# Revit family: Hager-FW-IP30-Without_Door-With_notch-vuoto-CH-it
name_source: partatom
category: Electrical Equipment
units: mm (PartAtom-declared; Revit-internal decimal feet)

## family parameters
Cut with Voids When Loaded = No
Host = Face
Panel Configuration = Two Columns, Circuits Across
Part Type = Panelboard
Room Calculation Point = No
Round Connector Dimension = Use Diameter
Shared = No

## types (16) — shared parameters
EF000003 - Tipo di montaggio = EV000128 - parete forata
EF000007 - colore = EV000202 - bianco
EF000049 - profondità = 125 mm  [stored 0.410105 ft]
EF000118 - con piastra di montaggio = No
EF000218 - profondità di incasso = 112 mm  [stored 0.367454 ft]
EF000339 - tipo di copertura = EV000494 - senza
EF001062 - esecuzione EMC = No
EF001088 - possibilità di applicazione = Yes
EF001131 - profondità interna = 112 mm  [stored 0.367454 ft]
EF001134 - barra DIN = Yes
EF001596 - Attacco Lampada = EV000179 - acciaio
EF004462 - tipo di chiusura = EV000154 - altri
EF005474 - grado di protezione (IP) = EV006410 - IP30
EF006244 - coperchio/porta trasparente = Yes
EF006306 - con serratura = No
EF009212 - esecuzione coperchio = EV009916 - con taglio
EF015776 - Morsettiera di terra = No
EF015777 - Morsettiera neutra = No
EF015941 - Segnale di passaggio porta = No
HG000002 - Con porta = No
HG000003 - Gamma = FW
HG000005 - Spessore = 3 mm  [stored 0.00984252 ft]
HG000006 - Ad incasso = Yes
HG000009 - Porta doppia a battente = No
HG000010 - Porte asimmetriche = No
HG000011 - File vuote nella parte basse = No
HG000017 - Distanza tra i poli = 18 mm  [stored 0.0590551 ft]
Manufacturer = Hager
Type Comments = FW
zero-valued in all types: Default Elevation, EF000266 - numero di file, EF002950 - Numero moduli DIN, HG000001 - Numero di colonne, HG000007 - Numero di colonne vuote, HG000008 - Numero di file vuote

## per-type parameters (varying)
| type | EF000008 - Larghezza | EF000040 - Altezza | EF000332 - Altezza della parte incassata | EF000846 - larghezza di montaggio | HG000004 - Codice produttore | Model |
| incassato IP30 L353 A1003 P125 0 Unità di divisione - FWU61L | 353 mm  [stored 1.15814 ft] | 1003 mm  [stored 3.29068 ft] | 952 mm  [stored 3.12336 ft] | 310 mm  [stored 1.01706 ft] | FWU61L | FWU61L |
| incassato IP30 L353 A1153 P125 0 Unità di divisione - FWU71L | 353 mm  [stored 1.15814 ft] | 1153 mm | 1102 mm  [stored 3.61549 ft] | 310 mm  [stored 1.01706 ft] | FWU71L | FWU71L |
| incassato IP30 L353 A1303 P125 0 Unità di divisione - FWU81L | 353 mm  [stored 1.15814 ft] | 1303 mm  [stored 4.27493 ft] | 1252 mm  [stored 4.10761 ft] | 310 mm  [stored 1.01706 ft] | FWU81L | FWU81L |
| incassato IP30 L353 A553 P125 0 Unità di divisione - FWU31L | 353 mm  [stored 1.15814 ft] | 553 mm  [stored 1.8143 ft] | 502 mm  [stored 1.64698 ft] | 310 mm  [stored 1.01706 ft] | FWU31L | FWU31L |
| incassato IP30 L353 A703 P125 0 Unità di divisione - FWU41L | 353 mm  [stored 1.15814 ft] | 703 mm  [stored 2.30643 ft] | 652 mm  [stored 2.13911 ft] | 310 mm  [stored 1.01706 ft] | FWU41L | FWU41L |
| incassato IP30 L353 A853 P125 0 Unità di divisione - FWU51L | 353 mm  [stored 1.15814 ft] | 853 mm  [stored 2.79856 ft] | 802 mm  [stored 2.63123 ft] | 310 mm  [stored 1.01706 ft] | FWU51L | FWU51L |
| incassato IP30 L603 A1003 P125 0 Unità di divisione - FWU62L | 603 mm | 1003 mm  [stored 3.29068 ft] | 952 mm  [stored 3.12336 ft] | 560 mm  [stored 1.83727 ft] | FWU62L | FWU62L |
| incassato IP30 L603 A1153 P125 0 Unità di divisione - FWU72L | 603 mm | 1153 mm | 1102 mm  [stored 3.61549 ft] | 560 mm  [stored 1.83727 ft] | FWU72L | FWU72L |
| incassato IP30 L603 A553 P125 0 Unità di divisione - FWU32L | 603 mm | 553 mm  [stored 1.8143 ft] | 502 mm  [stored 1.64698 ft] | 560 mm  [stored 1.83727 ft] | FWU32L | FWU32L |
| incassato IP30 L603 A703 P125 0 Unità di divisione - FWU42L | 603 mm | 703 mm  [stored 2.30643 ft] | 652 mm  [stored 2.13911 ft] | 560 mm  [stored 1.83727 ft] | FWU42L | FWU42L |
| incassato IP30 L603 A853 P125 0 Unità di divisione - FWU52L | 603 mm | 853 mm  [stored 2.79856 ft] | 802 mm  [stored 2.63123 ft] | 560 mm  [stored 1.83727 ft] | FWU52L | FWU52L |
| incassato IP30 L853 A1003 P125 0 Unità di divisione - FWU63L | 853 mm  [stored 2.79856 ft] | 1003 mm  [stored 3.29068 ft] | 952 mm  [stored 3.12336 ft] | 810 mm | FWU63L | FWU63L |
| incassato IP30 L853 A1153 P125 0 Unità di divisione - FWU73L | 853 mm  [stored 2.79856 ft] | 1153 mm | 1102 mm  [stored 3.61549 ft] | 810 mm | FWU73L | FWU73L |
| incassato IP30 L853 A553 P125 0 Unità di divisione - FWU33L | 853 mm  [stored 2.79856 ft] | 553 mm  [stored 1.8143 ft] | 502 mm  [stored 1.64698 ft] | 810 mm | FWU33L | FWU33L |
| incassato IP30 L853 A703 P125 0 Unità di divisione - FWU43L | 853 mm  [stored 2.79856 ft] | 703 mm  [stored 2.30643 ft] | 652 mm  [stored 2.13911 ft] | 810 mm | FWU43L | FWU43L |
| incassato IP30 L853 A853 P125 0 Unità di divisione - FWU53L | 853 mm  [stored 2.79856 ft] | 853 mm  [stored 2.79856 ft] | 802 mm  [stored 2.63123 ft] | 810 mm | FWU53L | FWU53L |

note: [stored X ft] marks values corroborated as IEEE doubles in the binary element streams (Revit-internal decimal feet)

## geometry (parser evidence)
native form markers: Sweep x17
no freeform markers — native parametric forms only
